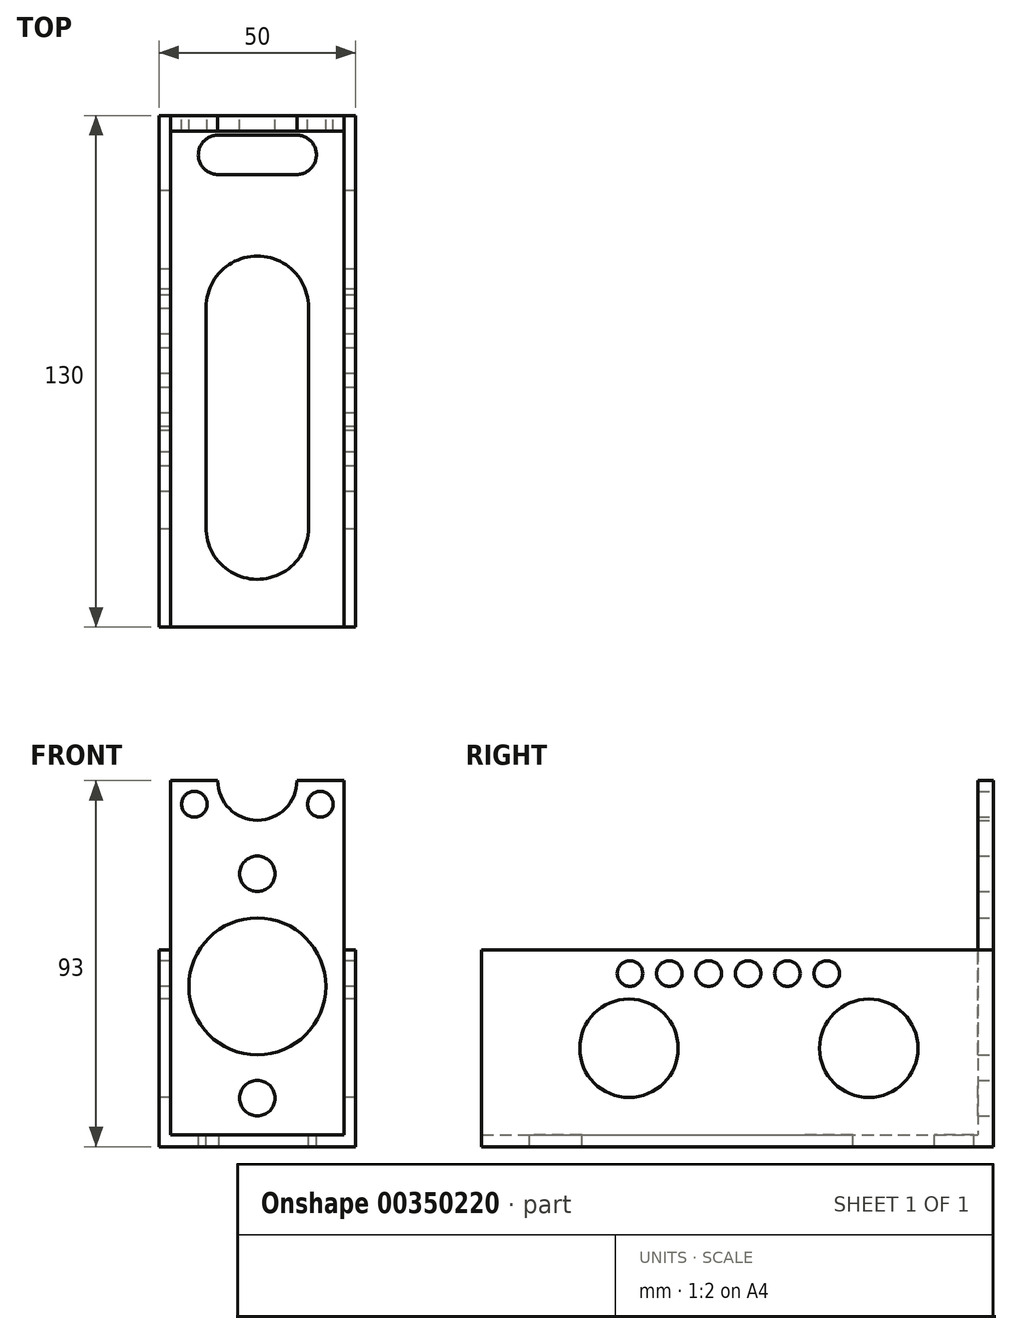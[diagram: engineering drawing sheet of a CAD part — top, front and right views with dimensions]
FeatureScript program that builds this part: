
annotation { "Feature Type Name" : "Feature", "Feature Type Description" : "" }
export const myFeature = defineFeature(function(context is Context, id is Id, definition is map)
    precondition{}
    {
        {
            var Q0;
            Q0=qCreatedBy(makeId("Front.planeOp"),FACE);
            var sketch = newSketch(context, id + "F0", { "sketchPlane" : qUnion([Q0])});
            skLineSegment(sketch, "E0.bottom", {"start": v(25, 25) * mm, "end": v(22, 25) * mm});
            skLineSegment(sketch, "E0.top", {"start": v(25, -25) * mm, "end": v(-25, -25) * mm});
            skLineSegment(sketch, "E0.left", {"start": v(25, 25) * mm, "end": v(25, -25) * mm});
            skLineSegment(sketch, "E0.right", {"start": v(-25, 25) * mm, "end": v(-25, -25) * mm});
            skPoint(sketch, "E0.middle", {"position": v(0, 0) * mm});
            skLineSegment(sketch, "E1", {"start": v(-22, 25) * mm, "end": v(-22, -22) * mm});
            skLineSegment(sketch, "E2", {"start": v(-22, -22) * mm, "end": v(22, -22) * mm});
            skLineSegment(sketch, "E3", {"start": v(22, -22) * mm, "end": v(22, 25) * mm});
            skLineSegment(sketch, "E4.trimOffspring", {"start": v(-22, 25) * mm, "end": v(-25, 25) * mm});
            skSolve(sketch);
        }
        {
            var Q0;
            Q0=makeQuery(id+"F0.imprint","IMPRINT",FACE,{"disambiguationData":[TD([[makeQuery(id+"F0.imprint","IMPRINT",EDGE,{"derivedFrom":sQuery(id+"F0.wireOp",EDGE,"E0.bottom")}),1.0]])]});
            extrude(context, id + "F1", {"entities" : qUnion([Q0]), "depth" : 130 * mm});
        }
        {
            var Q0;
            Q0=qCreatedBy(makeId("Front.planeOp"),FACE);
            var sketch = newSketch(context, id + "F2", { "sketchPlane" : qUnion([Q0])});
            skLineSegment(sketch, "E5", {"start": v(-22, -22) * mm, "end": v(-22, 25) * mm});
            skCircle(sketch, "E6", {"center": v(0, -12.67) * mm, "radius": 4.5 * mm});
            skCircle(sketch, "E7", {"center": v(0, 44.33) * mm, "radius": 4.5 * mm});
            skLineSegment(sketch, "E8.bottom", {"start": v(-22, 68) * mm, "end": v(-10.07, 68) * mm});
            skLineSegment(sketch, "E8.top", {"start": v(-22, -22) * mm, "end": v(22, -22) * mm});
            skLineSegment(sketch, "E8.left", {"start": v(-22, 68) * mm, "end": v(-22, -22) * mm});
            skLineSegment(sketch, "E8.right", {"start": v(22, 68) * mm, "end": v(22, -22) * mm});
            skPoint(sketch, "E8.middle", {"position": v(0, 23) * mm});
            skCircle(sketch, "E9", {"center": v(0, 15.73) * mm, "radius": 17.4 * mm});
            skArc(sketch, "E10", {"start": v(-10.07, 68) * mm, "mid": v(0, 57.93) * mm, "end": v(10.07, 68) * mm});
            skLineSegment(sketch, "E11.trimOffspring", {"start": v(10.07, 68) * mm, "end": v(22, 68) * mm});
            skCircle(sketch, "E12", {"center": v(-16, 62) * mm, "radius": 3.25 * mm});
            skCircle(sketch, "E13.MirrorC", {"center": v(16, 62) * mm, "radius": 3.25 * mm});
            skSolve(sketch);
        }
        {
            var Q0;
            Q0=makeQuery(id+"F2.imprint","IMPRINT",FACE,{"disambiguationData":[TD([[makeQuery(id+"F2.imprint","IMPRINT",EDGE,{"derivedFrom":sQuery(id+"F2.wireOp",EDGE,"E6")}),-1.0]])]});
            extrude(context, id + "F3", {"entities" : qUnion([Q0]), "operationType" : NewBodyOperationType.ADD, "depth" : 4 * mm});
        }
        {
            var Q0;
            Q0=qCreatedBy(makeId("Top.planeOp"),FACE);
            var sketch = newSketch(context, id + "F4", { "sketchPlane" : qUnion([Q0])});
            skPoint(sketch, "E14.middle", {"position": v(0, -9.64) * mm});
            skArc(sketch, "E15", {"start": v(-13, -104.58) * mm, "mid": v(-0.13, -117.85) * mm, "end": v(13, -104.85) * mm});
            skArc(sketch, "E16", {"start": v(13, -48.73) * mm, "mid": v(0, -35.73) * mm, "end": v(-13, -48.73) * mm});
            skLineSegment(sketch, "E17", {"start": v(-13, -104.58) * mm, "end": v(-13, -48.73) * mm});
            skLineSegment(sketch, "E18", {"start": v(13, -104.85) * mm, "end": v(13, -48.73) * mm});
            skArc(sketch, "E19", {"start": v(-9.95, -5) * mm, "mid": v(-15, -10.1) * mm, "end": v(-9.75, -15) * mm});
            skArc(sketch, "E20", {"start": v(10, -15) * mm, "mid": v(15, -10) * mm, "end": v(10, -5) * mm});
            skLineSegment(sketch, "E21", {"start": v(-10.25, -15) * mm, "end": v(10, -15) * mm});
            skLineSegment(sketch, "E22", {"start": v(-9.95, -5) * mm, "end": v(10, -5) * mm});
            skSolve(sketch);
        }
        {
            var Q0;
            Q0 = qSketchRegion(id + "F4", true);
            var Q1;
            Q1=makeQuery(id+"F1.opExtrude","SWEPT_FACE",FACE,{"disambiguationData":[OSD([sQuery(id+"F0.wireOp",EDGE,"E0.top")])]});
            extrude(context, id + "F5", {"entities" : qUnion([Q0, Q1]), "operationType" : NewBodyOperationType.REMOVE, "endBound" : BoundingType.THROUGH_ALL, "oppositeDirection" : true, "depth" : 25 * mm});
        }
        {
            var Q0;
            Q0=makeQuery(id+"F1.opExtrude","SWEPT_FACE",FACE,{"disambiguationData":[OSD([sQuery(id+"F0.wireOp",EDGE,"E0.right")])]});
            var sketch = newSketch(context, id + "F6", { "sketchPlane" : qUnion([Q0])});
            skSolve(sketch);
        }
        {
            var Q0;
            {var subQ0=sQuery(id+"F0.wireOp",EDGE,"E0.right");Q0=makeQuery(id+"F6.imprint","IMPRINT",FACE,{"disambiguationData":[TD([[makeQuery(id+"F6.imprint","IMPRINT",EDGE,{"derivedFrom":makeQuery(id+"F1.opExtrude","CAP_EDGE",EDGE,{"disambiguationData":[OSD([subQ0])],"isStart":true})}),1.0]])]});}
            var sketch = newSketch(context, id + "F7", { "sketchPlane" : qUnion([Q0])});
            skCircle(sketch, "E23", {"center": v(92.59, 0) * mm, "radius": 12.5 * mm});
            skCircle(sketch, "E24", {"center": v(31.65, 0) * mm, "radius": 12.5 * mm});
            skCircle(sketch, "E25", {"center": v(92.33, 19) * mm, "radius": 3.25 * mm});
            skCircle(sketch, "E26", {"center": v(82.33, 19) * mm, "radius": 3.25 * mm});
            skCircle(sketch, "E27", {"center": v(72.33, 19) * mm, "radius": 3.25 * mm});
            skCircle(sketch, "E28", {"center": v(62.33, 19) * mm, "radius": 3.25 * mm});
            skCircle(sketch, "E29", {"center": v(52.33, 19) * mm, "radius": 3.25 * mm});
            skCircle(sketch, "E30", {"center": v(42.33, 19) * mm, "radius": 3.25 * mm});
            skSolve(sketch);
        }
        {
            var Q0;
            Q0=makeQuery(id+"F7.imprint","IMPRINT",FACE,{"disambiguationData":[TD([[makeQuery(id+"F7.imprint","IMPRINT",EDGE,{"derivedFrom":sQuery(id+"F7.wireOp",EDGE,"E24")}),1.0]])]});
            var Q1;
            Q1=makeQuery(id+"F7.imprint","IMPRINT",FACE,{"disambiguationData":[TD([[makeQuery(id+"F7.imprint","IMPRINT",EDGE,{"derivedFrom":sQuery(id+"F7.wireOp",EDGE,"E23")}),1.0]])]});
            var Q2;
            Q2=sQuery(id+"F7.wireOp",EDGE,"E24");
            var Q3;
            Q3=sQuery(id+"F7.wireOp",EDGE,"E23");
            extrude(context, id + "F8", {"entities" : qUnion([Q0, Q1]), "operationType" : NewBodyOperationType.REMOVE, "surfaceEntities" : qUnion([Q2, Q3]), "endBound" : BoundingType.THROUGH_ALL, "oppositeDirection" : true, "depth" : 25 * mm});
        }
        {
            var Q0;
            Q0 = qSketchRegion(id + "F7", true);
            extrude(context, id + "F9", {"entities" : qUnion([Q0]), "operationType" : NewBodyOperationType.REMOVE, "endBound" : BoundingType.THROUGH_ALL, "oppositeDirection" : true, "depth" : 25 * mm});
        }
    });
